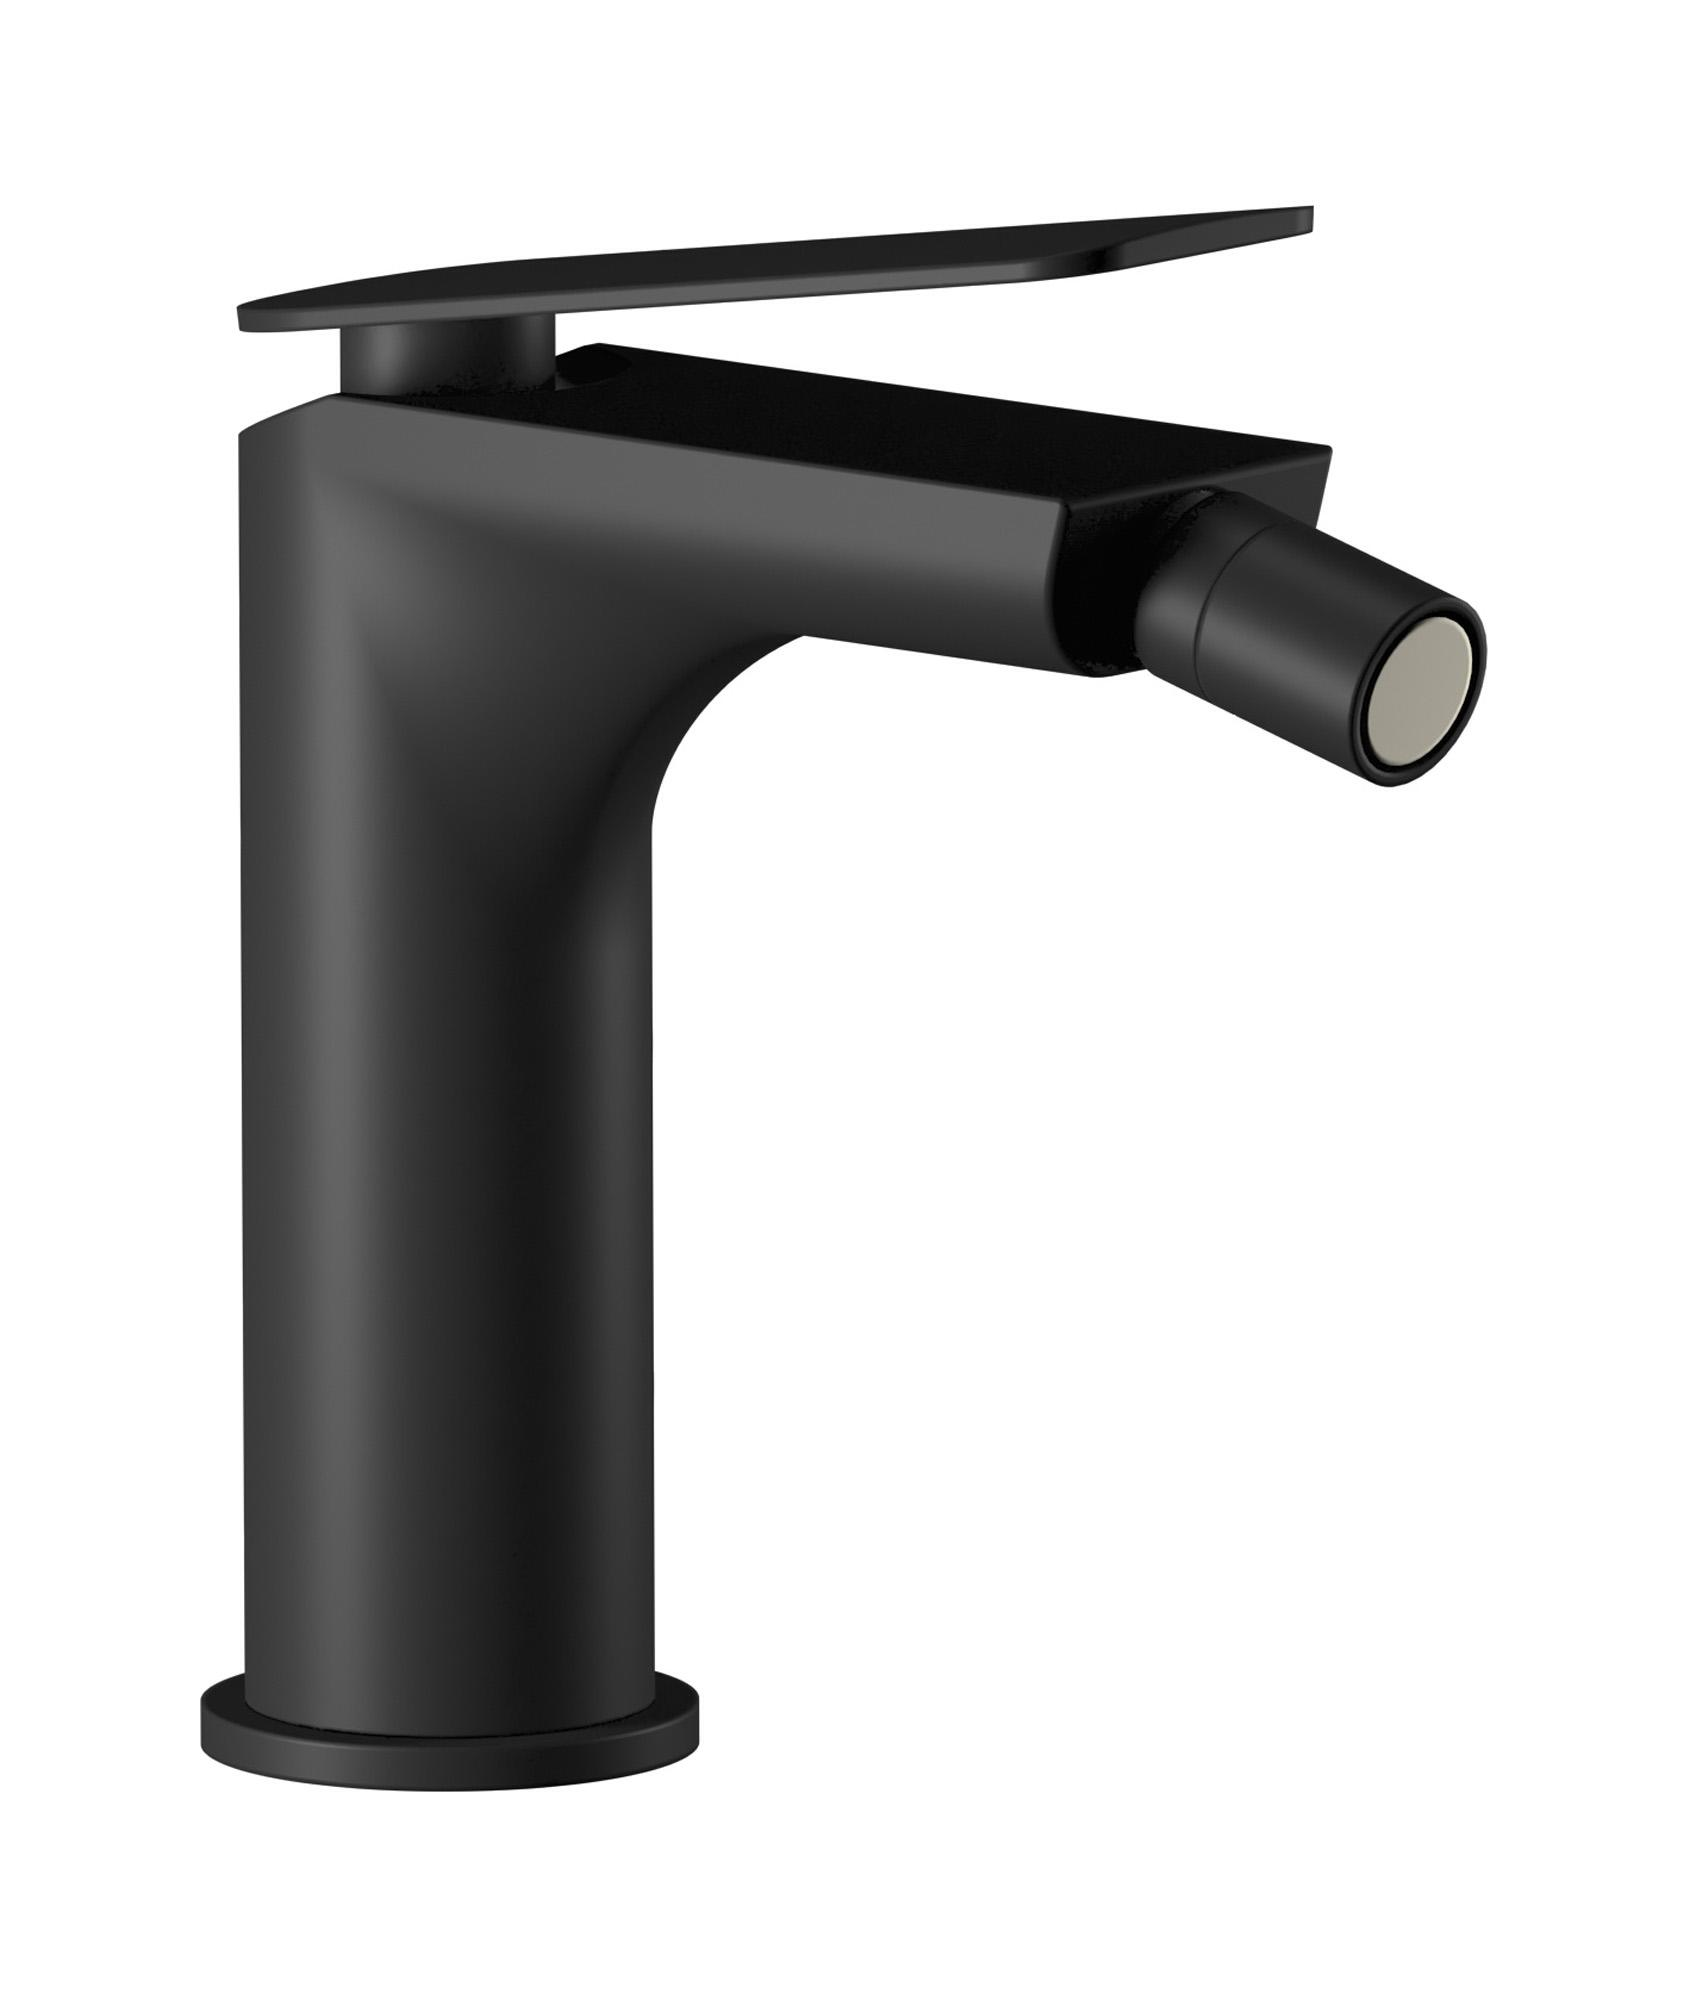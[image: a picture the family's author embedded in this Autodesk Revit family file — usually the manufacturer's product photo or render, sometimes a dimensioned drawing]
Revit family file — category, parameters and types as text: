
# Revit family: K2220
name_source: partatom
category: Apparecchi idraulici
units: mm (PartAtom-declared; Revit-internal decimal feet)

## family parameters
Basato su piano di lavoro = No
Condiviso = No
Mantieni orientamento annotazione = No
Numero OmniClass = 23.45.55.17
Punto di calcolo locali = No
Quota connettore circolare = Usa diametro
Sempre verticale = Sì
Taglio con vuoti quando caricato = No
Tipo di parte = Normale
Titolo OmniClass = Mixing Faucets

## types (9) — shared parameters
Cold water inlet = 10 mm  [stored 0.0328084 ft]
Commenti sul tipo = Bidet mixer
Connessione CW = No
Connessione HW = No
Connessione di scarico = No
Connessione di ventilazione = No
Descrizione = Monohole bidet mixer complete with drain
Hot water inlet = 10 mm  [stored 0.0328084 ft]
Produttore = IB Rubinetterie S.p.A.
URL = https://www.weareib.it
zero-valued in all types: Prospetto di default

## per-type parameters (varying)
| type | Finishes surface | Immagine tipo | Modello |
| Chrome | IB_Chrome | K2220CC.jpg | K2220CC |
| Platinum | IB_Platinum | K2220PL.jpg | K2220PL |
| Brushed nickel | IB_Brushed nickel | K2220SS.jpg | K2220SS |
| Matt black | IB_matt black | K2220NP.jpg | K2220NP |
| Matt white | IB_matt white | K2220BO.jpg | K2220BO |
| Pale gold | IB_Pale gold | K2220II.jpg | K2220II |
| Brushed pale gold | IB_brushed pale gold | K2220IS.jpg | K2220IS |
| Rose gold | IB_Rose gold | K2220RS.jpg | K2220RS |
| Gold | IB_gold | K2220OO.jpg | K2220OO |

note: [stored X ft] marks values corroborated as IEEE doubles in the binary element streams (Revit-internal decimal feet)
